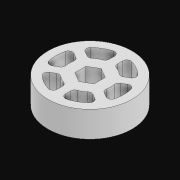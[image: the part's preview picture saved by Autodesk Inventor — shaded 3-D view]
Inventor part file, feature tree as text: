
AUTODESK INVENTOR PART (.ipt)
format: ipt  version: 2021 (Build 250183000, 183)  size: 336,896 bytes
history: native  units: in
note: dims shown in document units (in); Inventor stores cm internally (conversion verified against a paired STEP export)
features: other x9, extrude x2, sketch x2, projected_geometry x2
ambient origin geometry x8: Origin, YZ Plane, XZ Plane, XY Plane, X Axis, Y Axis, Z Axis, Center Point
bodies: Solid1 (feature_tree)
feature tree (15):
  other  "Table"
  other  "Color = 60a Flex Wheel"
  other  "Color = 30a Flex Wheel"
  other  "Color = 40a Flex Wheel"
  other  "Thickness = 0.250 in"
  other  "Thickness = 0.500 in"
  other  "Thickness = 0.125 in"
  other  "Thickness = 0.375 in"
  extrude  "Extrusion1"  Depth=0.5in TaperAngle=0.0deg
  extrude  "Extrusion2"  [1 undecoded]
  sketch  "Sketch1"  dims[d1=0.0in d2=0.5in d3=0.0in]
  projected_geometry  "Projected Loop1"
  sketch  "Sketch2"
  projected_geometry  "Projected Loop2"
  other  "Cut-Extrude2"
note: 1 required parameter value undecoded (feature->parameter linkage not recoverable at this tier; creation-order binding heuristic only, values carry confidence <= 0.55)
